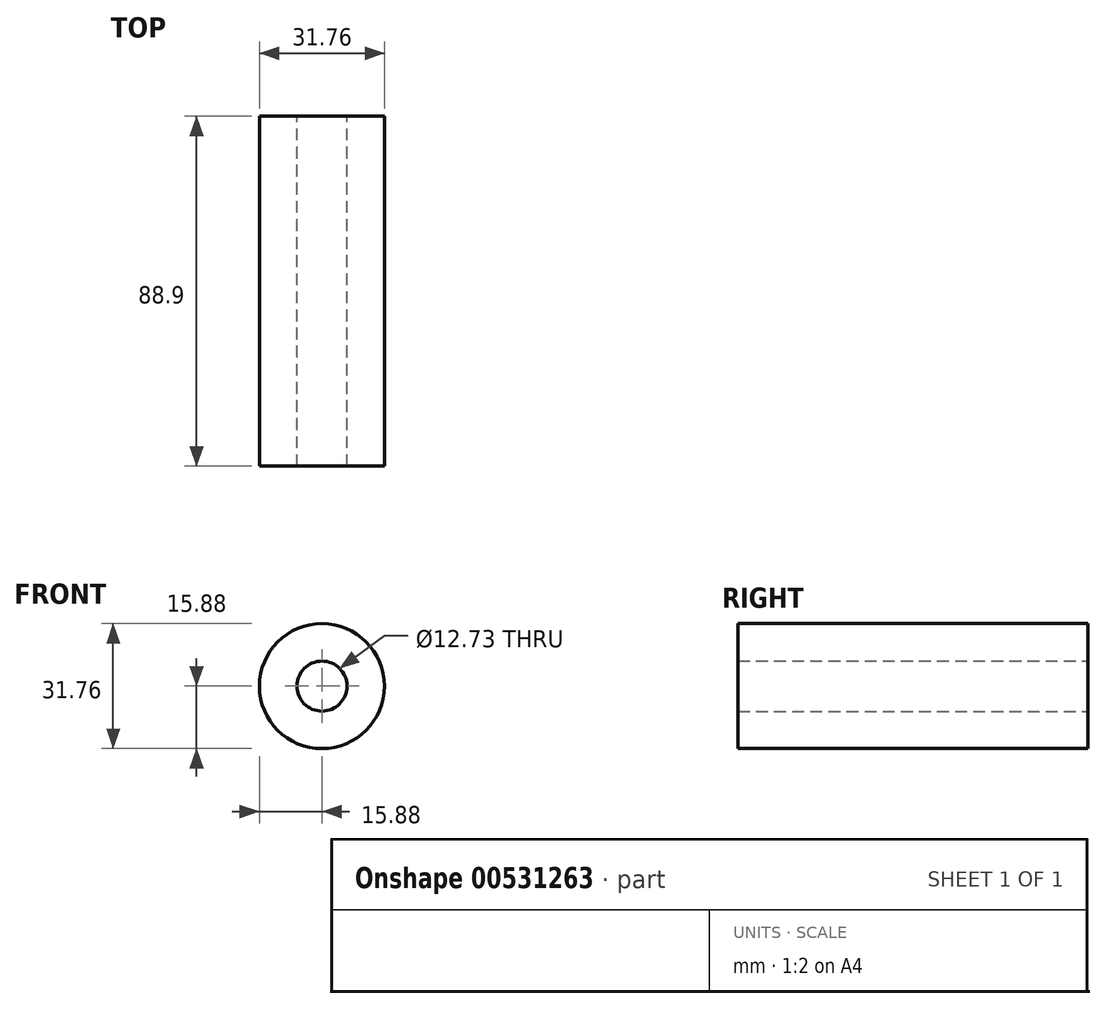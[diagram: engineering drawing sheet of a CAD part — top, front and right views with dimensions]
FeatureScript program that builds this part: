
annotation { "Feature Type Name" : "Feature", "Feature Type Description" : "" }
export const myFeature = defineFeature(function(context is Context, id is Id, definition is map)
    precondition{}
    {
        {
            var Q0;
            Q0=qCreatedBy(makeId("Front.planeOp"),FACE);
            var sketch = newSketch(context, id + "F0", { "sketchPlane" : qUnion([Q0])});
            skCircle(sketch, "E0", {"center": v(0, 0) * mm, "radius": 15.88 * mm});
            skCircle(sketch, "E1", {"center": v(0, 0) * mm, "radius": 6.36 * mm});
            skSolve(sketch);
        }
        {
            var Q0;
            Q0=makeQuery(id+"F0.imprint","IMPRINT",FACE,{"disambiguationData":[TD([[makeQuery(id+"F0.imprint","IMPRINT",EDGE,{"derivedFrom":sQuery(id+"F0.wireOp",EDGE,"E0")}),1.0]])]});
            extrude(context, id + "F1", {"entities" : qUnion([Q0]), "depth" : 88.9 * mm, "offsetDistance" : 25.4 * mm});
        }
    });
